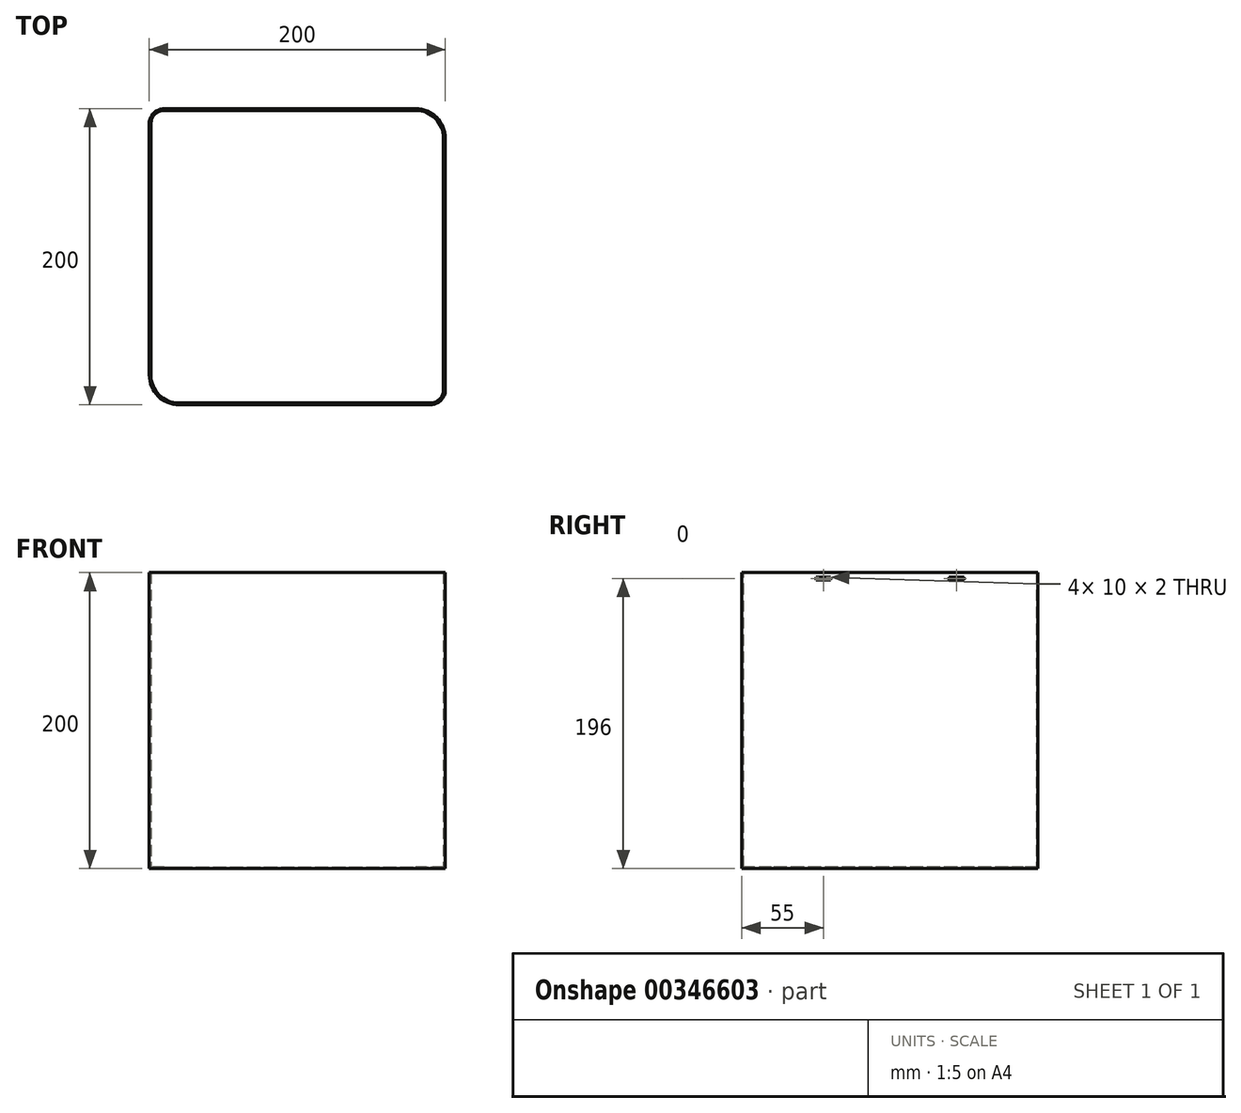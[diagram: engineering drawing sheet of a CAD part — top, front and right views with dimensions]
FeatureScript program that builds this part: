
annotation { "Feature Type Name" : "Feature", "Feature Type Description" : "" }
export const myFeature = defineFeature(function(context is Context, id is Id, definition is map)
    precondition{}
    {
        {
            var Q0;
            Q0=qCreatedBy(makeId("Top.planeOp"),FACE);
            var sketch = newSketch(context, id + "F0", { "sketchPlane" : qUnion([Q0])});
            skLineSegment(sketch, "E0.bottom", {"start": v(-90, 100) * mm, "end": v(80, 100) * mm});
            skLineSegment(sketch, "E0.top", {"start": v(-80, -100) * mm, "end": v(90, -100) * mm});
            skLineSegment(sketch, "E0.left", {"start": v(-100, 90) * mm, "end": v(-100, -80) * mm});
            skLineSegment(sketch, "E0.right", {"start": v(100, 80) * mm, "end": v(100, -90) * mm});
            skPoint(sketch, "E1.visualSharp", {"position": v(-100, 100) * mm});
            skArc(sketch, "E1.filletArc", {"start": v(-90, 100) * mm, "mid": v(-97.07, 97.07) * mm, "end": v(-100, 90) * mm});
            skPoint(sketch, "E2.visualSharp", {"position": v(-100, -100) * mm});
            skArc(sketch, "E2.filletArc", {"start": v(-100, -80) * mm, "mid": v(-94.14, -94.14) * mm, "end": v(-80, -100) * mm});
            skPoint(sketch, "E3.visualSharp", {"position": v(100, -100) * mm});
            skArc(sketch, "E3.filletArc", {"start": v(90, -100) * mm, "mid": v(97.07, -97.07) * mm, "end": v(100, -90) * mm});
            skPoint(sketch, "E4.visualSharp", {"position": v(100, 100) * mm});
            skArc(sketch, "E4.filletArc", {"start": v(100, 80) * mm, "mid": v(94.14, 94.14) * mm, "end": v(80, 100) * mm});
            skLineSegment(sketch, "E5", {"start": v(100, -100) * mm, "end": v(-100, 100) * mm});
            skLineSegment(sketch, "E6", {"start": v(100, 100) * mm, "end": v(-100, -100) * mm});
            skPoint(sketch, "E7", {"position": v(0, 0) * mm});
            skSolve(sketch);
        }
        {
            var Q0;
            Q0=makeQuery(id+"F0.imprint","IMPRINT",FACE,{"disambiguationData":[TD([[makeQuery(id+"F0.imprint","IMPRINT",EDGE,{"derivedFrom":sQuery(id+"F0.wireOp",EDGE,"E0.bottom")}),-1.0]])]});
            var Q1;
            {var subQ6=sQuery(id+"F0.wireOp",EDGE,"E0.right");Q1=makeQuery(id+"F0.imprint","IMPRINT",FACE,{"disambiguationData":[TD([[makeQuery(id+"F0.imprint","IMPRINT",EDGE,{"derivedFrom":subQ6}),-1.0]])]});}
            var Q2;
            {var subQ1=sQuery(id+"F0.wireOp",EDGE,"E0.top");Q2=makeQuery(id+"F0.imprint","IMPRINT",FACE,{"disambiguationData":[TD([[makeQuery(id+"F0.imprint","IMPRINT",EDGE,{"derivedFrom":subQ1}),1.0]])]});}
            var Q3;
            {var subQ5=sQuery(id+"F0.wireOp",EDGE,"E0.left");Q3=makeQuery(id+"F0.imprint","IMPRINT",FACE,{"disambiguationData":[TD([[makeQuery(id+"F0.imprint","IMPRINT",EDGE,{"derivedFrom":subQ5}),1.0]])]});}
            extrude(context, id + "F1", {"entities" : qUnion([Q0, Q1, Q2, Q3]), "depth" : 200 * mm});
        }
        {
            var Q0;
            Q0=makeQuery(id+"F1.opExtrude","CAP_FACE",FACE,{"disambiguationData":[OSD([sQuery(id+"F0.wireOp",EDGE,"E0.bottom"),sQuery(id+"F0.wireOp",EDGE,"E0.top"),sQuery(id+"F0.wireOp",EDGE,"E0.left"),sQuery(id+"F0.wireOp",EDGE,"E0.right"),sQuery(id+"F0.wireOp",EDGE,"E1.filletArc"),sQuery(id+"F0.wireOp",EDGE,"E2.filletArc"),sQuery(id+"F0.wireOp",EDGE,"E3.filletArc"),sQuery(id+"F0.wireOp",EDGE,"E4.filletArc")])],"isStart":false});
            shell(context, id + "F2", {"entities" : qUnion([Q0]), "thickness" : 1.2 * mm});
        }
        {
            var Q0;
            Q0=makeQuery(id+"F1.opExtrude","SWEPT_FACE",FACE,{"disambiguationData":[OSD([sQuery(id+"F0.wireOp",EDGE,"E0.left")])]});
            var sketch = newSketch(context, id + "F3", { "sketchPlane" : qUnion([Q0])});
            skLineSegment(sketch, "E8.bottom", {"start": v(-40, 197) * mm, "end": v(-50, 197) * mm});
            skLineSegment(sketch, "E8.top", {"start": v(-40, 195) * mm, "end": v(-50, 195) * mm});
            skLineSegment(sketch, "E8.left", {"start": v(-40, 197) * mm, "end": v(-40, 195) * mm});
            skLineSegment(sketch, "E8.right", {"start": v(-50, 197) * mm, "end": v(-50, 195) * mm});
            skLineSegment(sketch, "E9", {"start": v(0, 200) * mm, "end": v(0, 0) * mm});
            skLineSegment(sketch, "E10.MirrorCS", {"start": v(50, 197) * mm, "end": v(50, 195) * mm});
            skLineSegment(sketch, "E11.MirrorCS", {"start": v(40, 197) * mm, "end": v(40, 195) * mm});
            skLineSegment(sketch, "E12.MirrorCS", {"start": v(40, 197) * mm, "end": v(50, 197) * mm});
            skLineSegment(sketch, "E13.MirrorCS", {"start": v(40, 195) * mm, "end": v(50, 195) * mm});
            skSolve(sketch);
        }
        {
            var Q0;
            Q0=makeQuery(id+"F3.imprint","IMPRINT",FACE,{"disambiguationData":[TD([[makeQuery(id+"F3.imprint","IMPRINT",EDGE,{"derivedFrom":sQuery(id+"F3.wireOp",EDGE,"E8.bottom")}),1.0]])]});
            var Q1;
            Q1=makeQuery(id+"F3.imprint","IMPRINT",FACE,{"disambiguationData":[TD([[makeQuery(id+"F3.imprint","IMPRINT",EDGE,{"derivedFrom":sQuery(id+"F3.wireOp",EDGE,"E10.MirrorCS")}),-1.0]])]});
            extrude(context, id + "F4", {"entities" : qUnion([Q0, Q1]), "endBound" : BoundingType.UP_TO_NEXT, "oppositeDirection" : true, "depth" : 25 * mm});
        }
        {
            var Q0;
            Q0=makeQuery(id+"F4.opExtrude","SWEPT_BODY",BODY,{"disambiguationData":[OSD([sQuery(id+"F3.wireOp",EDGE,"E8.bottom"),sQuery(id+"F3.wireOp",EDGE,"E8.top"),sQuery(id+"F3.wireOp",EDGE,"E8.left"),sQuery(id+"F3.wireOp",EDGE,"E8.right")])]});
            var Q1;
            Q1=makeQuery(id+"F4.opExtrude","SWEPT_BODY",BODY,{"disambiguationData":[OSD([sQuery(id+"F3.wireOp",EDGE,"E10.MirrorCS"),sQuery(id+"F3.wireOp",EDGE,"E11.MirrorCS"),sQuery(id+"F3.wireOp",EDGE,"E12.MirrorCS"),sQuery(id+"F3.wireOp",EDGE,"E13.MirrorCS")])]});
            var Q2;
            Q2=qCreatedBy(makeId("Right.planeOp"),FACE);
            mirror(context, id + "F5", {"entities" : qUnion([Q0, Q1]), "mirrorPlane" : qUnion([Q2])});
        }
        {
            var Q0;
            Q0=makeQuery(id+"F4.opExtrude","SWEPT_BODY",BODY,{"disambiguationData":[OSD([sQuery(id+"F3.wireOp",EDGE,"E8.bottom"),sQuery(id+"F3.wireOp",EDGE,"E8.top"),sQuery(id+"F3.wireOp",EDGE,"E8.left"),sQuery(id+"F3.wireOp",EDGE,"E8.right")])]});
            var Q1;
            Q1=makeQuery(id+"F4.opExtrude","SWEPT_BODY",BODY,{"disambiguationData":[OSD([sQuery(id+"F3.wireOp",EDGE,"E10.MirrorCS"),sQuery(id+"F3.wireOp",EDGE,"E11.MirrorCS"),sQuery(id+"F3.wireOp",EDGE,"E12.MirrorCS"),sQuery(id+"F3.wireOp",EDGE,"E13.MirrorCS")])]});
            var Q2;
            Q2=makeQuery(id+"F5.opPattern","COPY",BODY,{"derivedFrom":makeQuery(id+"F4.opExtrude","SWEPT_BODY",BODY,{"disambiguationData":[OSD([sQuery(id+"F3.wireOp",EDGE,"E10.MirrorCS"),sQuery(id+"F3.wireOp",EDGE,"E11.MirrorCS"),sQuery(id+"F3.wireOp",EDGE,"E12.MirrorCS"),sQuery(id+"F3.wireOp",EDGE,"E13.MirrorCS")])]}),"instanceName":"1"});
            var Q3;
            Q3=makeQuery(id+"F5.opPattern","COPY",BODY,{"derivedFrom":makeQuery(id+"F4.opExtrude","SWEPT_BODY",BODY,{"disambiguationData":[OSD([sQuery(id+"F3.wireOp",EDGE,"E8.bottom"),sQuery(id+"F3.wireOp",EDGE,"E8.top"),sQuery(id+"F3.wireOp",EDGE,"E8.left"),sQuery(id+"F3.wireOp",EDGE,"E8.right")])]}),"instanceName":"1"});
            var Q4;
            Q4=makeQuery(id+"F1.opExtrude","SWEPT_BODY",BODY,{"disambiguationData":[OSD([sQuery(id+"F0.wireOp",EDGE,"E0.bottom"),sQuery(id+"F0.wireOp",EDGE,"E0.top"),sQuery(id+"F0.wireOp",EDGE,"E0.left"),sQuery(id+"F0.wireOp",EDGE,"E0.right"),sQuery(id+"F0.wireOp",EDGE,"E1.filletArc"),sQuery(id+"F0.wireOp",EDGE,"E2.filletArc"),sQuery(id+"F0.wireOp",EDGE,"E3.filletArc"),sQuery(id+"F0.wireOp",EDGE,"E4.filletArc")])]});
            booleanBodies(context, id + "F6", {"operationType" : BooleanOperationType.SUBTRACTION, "tools" : qUnion([Q0, Q1, Q2, Q3]), "targets" : qUnion([Q4])});
        }
    });
